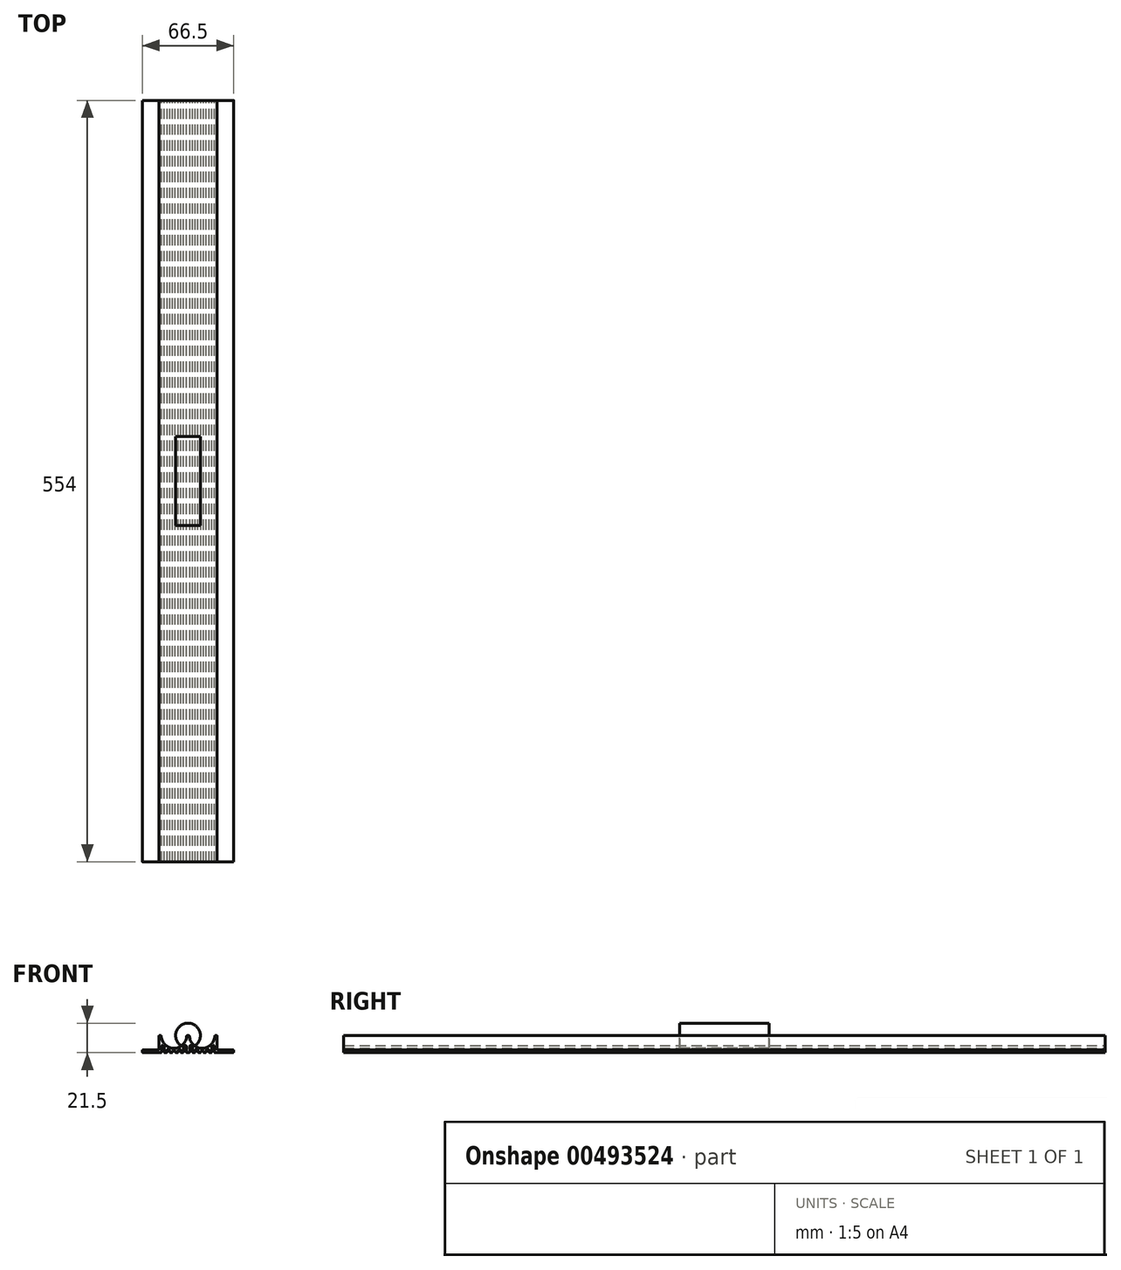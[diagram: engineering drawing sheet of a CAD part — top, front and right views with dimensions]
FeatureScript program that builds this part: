
annotation { "Feature Type Name" : "Feature", "Feature Type Description" : "" }
export const myFeature = defineFeature(function(context is Context, id is Id, definition is map)
    precondition{}
    {
        {
            var Q0;
            Q0=qCreatedBy(makeId("Front.planeOp"),FACE);
            var sketch = newSketch(context, id + "F0", { "sketchPlane" : qUnion([Q0])});
            skArc(sketch, "E0", {"start": v(-19.49, -0.47) * mm, "mid": v(-10.25, -9.25) * mm, "end": v(-1.01, -0.47) * mm});
            skArc(sketch, "E1", {"start": v(-18.38, -7.4) * mm, "mid": v(-17.92, -7.89) * mm, "end": v(-17.42, -8.34) * mm});
            skLineSegment(sketch, "E2", {"start": v(-21.25, -0.5) * mm, "end": v(-21.25, -10) * mm});
            skLineSegment(sketch, "E3", {"start": v(-21.25, -12.5) * mm, "end": v(-19.75, -12.5) * mm});
            skLineSegment(sketch, "E4", {"start": v(-19.25, -7.75) * mm, "end": v(-19.25, -12) * mm});
            skLineSegment(sketch, "E5", {"start": v(-17.25, -8.72) * mm, "end": v(-17.25, -12) * mm});
            skLineSegment(sketch, "E6", {"start": v(-15.25, -10.58) * mm, "end": v(-15.25, -12) * mm});
            skLineSegment(sketch, "E7", {"start": v(-13.25, -10.95) * mm, "end": v(-13.25, -12) * mm});
            skLineSegment(sketch, "E8", {"start": v(-11.25, -11.49) * mm, "end": v(-11.25, -12) * mm});
            skLineSegment(sketch, "E9", {"start": v(-1.25, -7.75) * mm, "end": v(-1.25, -12) * mm});
            skLineSegment(sketch, "E10.trimOffspring", {"start": v(-16.75, -12.5) * mm, "end": v(-15.75, -12.5) * mm});
            skLineSegment(sketch, "E11.trimOffspring", {"start": v(-12.75, -12.5) * mm, "end": v(-11.75, -12.5) * mm});
            skLineSegment(sketch, "E12.trimOffspring", {"start": v(-0.75, -12.5) * mm, "end": v(0, -12.5) * mm});
            skLineSegment(sketch, "E13", {"start": v(-20.75, 0) * mm, "end": v(-19.99, 0) * mm});
            skLineSegment(sketch, "E14", {"start": v(-10.25, 0) * mm, "end": v(0, 0) * mm, "construction": true});
            skArc(sketch, "E15.trimOffspring", {"start": v(-14.55, -10.12) * mm, "mid": v(-14.08, -10.31) * mm, "end": v(-13.6, -10.48) * mm});
            skArc(sketch, "E16.trimOffspring", {"start": v(-10.73, -10.99) * mm, "mid": v(-10.25, -11) * mm, "end": v(-9.77, -10.99) * mm});
            skLineSegment(sketch, "E17", {"start": v(-0.51, 0) * mm, "end": v(0, 0) * mm});
            skLineSegment(sketch, "E18", {"start": v(-9.25, -11.49) * mm, "end": v(-9.25, -12) * mm});
            skLineSegment(sketch, "E19", {"start": v(-8.75, -12.5) * mm, "end": v(-7.75, -12.5) * mm});
            skLineSegment(sketch, "E20", {"start": v(-7.25, -12) * mm, "end": v(-7.25, -10.95) * mm});
            skLineSegment(sketch, "E21", {"start": v(-5.25, -10.58) * mm, "end": v(-5.25, -12) * mm});
            skLineSegment(sketch, "E22", {"start": v(-4.75, -12.5) * mm, "end": v(-3.75, -12.5) * mm});
            skLineSegment(sketch, "E23", {"start": v(-3.25, -12) * mm, "end": v(-3.25, -8.72) * mm});
            skLineSegment(sketch, "E24", {"start": v(-19.25, -12.5) * mm, "end": v(-17.25, -12.5) * mm, "construction": true});
            skLineSegment(sketch, "E25", {"start": v(-15.25, -12.5) * mm, "end": v(-13.25, -12.5) * mm, "construction": true});
            skLineSegment(sketch, "E26", {"start": v(-11.25, -12.5) * mm, "end": v(-9.25, -12.5) * mm, "construction": true});
            skLineSegment(sketch, "E27", {"start": v(-7.25, -12.5) * mm, "end": v(-5.25, -12.5) * mm, "construction": true});
            skLineSegment(sketch, "E28", {"start": v(-3.25, -12.5) * mm, "end": v(-1.25, -12.5) * mm, "construction": true});
            skArc(sketch, "E29.trimOffspring", {"start": v(-6.9, -10.48) * mm, "mid": v(-6.42, -10.31) * mm, "end": v(-5.95, -10.12) * mm});
            skArc(sketch, "E30.trimOffspring", {"start": v(-3.08, -8.34) * mm, "mid": v(-2.58, -7.89) * mm, "end": v(-2.12, -7.4) * mm});
            skLineSegment(sketch, "E31", {"start": v(-21.25, -12.5) * mm, "end": v(-32.75, -12.5) * mm});
            skLineSegment(sketch, "E32", {"start": v(-33.25, -12) * mm, "end": v(-33.25, -11) * mm});
            skLineSegment(sketch, "E33", {"start": v(-32.75, -10.5) * mm, "end": v(-21.75, -10.5) * mm});
            skPoint(sketch, "E34.visualSharp", {"position": v(-21.25, -10.5) * mm});
            skArc(sketch, "E34.filletArc", {"start": v(-21.75, -10.5) * mm, "mid": v(-21.4, -10.35) * mm, "end": v(-21.25, -10) * mm});
            skPoint(sketch, "E35.visualSharp", {"position": v(-19.25, -12.5) * mm});
            skArc(sketch, "E35.filletArc", {"start": v(-19.75, -12.5) * mm, "mid": v(-19.4, -12.35) * mm, "end": v(-19.25, -12) * mm});
            skPoint(sketch, "E36.visualSharp", {"position": v(-17.25, -12.5) * mm});
            skArc(sketch, "E36.filletArc", {"start": v(-17.25, -12) * mm, "mid": v(-17.1, -12.35) * mm, "end": v(-16.75, -12.5) * mm});
            skPoint(sketch, "E37.visualSharp", {"position": v(-19.25, -6.32) * mm});
            skArc(sketch, "E37.filletArc", {"start": v(-18.38, -7.4) * mm, "mid": v(-18.93, -7.28) * mm, "end": v(-19.25, -7.75) * mm});
            skPoint(sketch, "E38.visualSharp", {"position": v(-17.25, -8.49) * mm});
            skArc(sketch, "E38.filletArc", {"start": v(-17.25, -8.72) * mm, "mid": v(-17.3, -8.5) * mm, "end": v(-17.42, -8.34) * mm});
            skPoint(sketch, "E39.visualSharp", {"position": v(-15.25, -9.8) * mm});
            skArc(sketch, "E39.filletArc", {"start": v(-14.55, -10.12) * mm, "mid": v(-15.03, -10.17) * mm, "end": v(-15.25, -10.58) * mm});
            skPoint(sketch, "E40.visualSharp", {"position": v(-13.25, -10.58) * mm});
            skArc(sketch, "E40.filletArc", {"start": v(-13.25, -10.95) * mm, "mid": v(-13.35, -10.66) * mm, "end": v(-13.6, -10.48) * mm});
            skPoint(sketch, "E41.visualSharp", {"position": v(-15.25, -12.5) * mm});
            skArc(sketch, "E41.filletArc", {"start": v(-15.75, -12.5) * mm, "mid": v(-15.4, -12.35) * mm, "end": v(-15.25, -12) * mm});
            skPoint(sketch, "E42.visualSharp", {"position": v(-13.25, -12.5) * mm});
            skArc(sketch, "E42.filletArc", {"start": v(-13.25, -12) * mm, "mid": v(-13.1, -12.35) * mm, "end": v(-12.75, -12.5) * mm});
            skPoint(sketch, "E43.visualSharp", {"position": v(-11.25, -12.5) * mm});
            skArc(sketch, "E43.filletArc", {"start": v(-11.75, -12.5) * mm, "mid": v(-11.4, -12.35) * mm, "end": v(-11.25, -12) * mm});
            skPoint(sketch, "E44.visualSharp", {"position": v(-11.25, -10.95) * mm});
            skArc(sketch, "E44.filletArc", {"start": v(-10.73, -10.99) * mm, "mid": v(-11.1, -11.13) * mm, "end": v(-11.25, -11.49) * mm});
            skPoint(sketch, "E45.visualSharp", {"position": v(-9.25, -10.95) * mm});
            skArc(sketch, "E45.filletArc", {"start": v(-9.25, -11.49) * mm, "mid": v(-9.4, -11.13) * mm, "end": v(-9.77, -10.99) * mm});
            skPoint(sketch, "E46.visualSharp", {"position": v(-9.25, -12.5) * mm});
            skArc(sketch, "E46.filletArc", {"start": v(-9.25, -12) * mm, "mid": v(-9.1, -12.35) * mm, "end": v(-8.75, -12.5) * mm});
            skPoint(sketch, "E47.visualSharp", {"position": v(-7.25, -12.5) * mm});
            skArc(sketch, "E47.filletArc", {"start": v(-7.75, -12.5) * mm, "mid": v(-7.4, -12.35) * mm, "end": v(-7.25, -12) * mm});
            skPoint(sketch, "E48.visualSharp", {"position": v(-7.25, -10.58) * mm});
            skArc(sketch, "E48.filletArc", {"start": v(-6.9, -10.48) * mm, "mid": v(-7.15, -10.66) * mm, "end": v(-7.25, -10.95) * mm});
            skPoint(sketch, "E49.visualSharp", {"position": v(-5.25, -9.8) * mm});
            skArc(sketch, "E49.filletArc", {"start": v(-5.25, -10.58) * mm, "mid": v(-5.47, -10.17) * mm, "end": v(-5.95, -10.12) * mm});
            skPoint(sketch, "E50.visualSharp", {"position": v(-5.25, -12.5) * mm});
            skArc(sketch, "E50.filletArc", {"start": v(-5.25, -12) * mm, "mid": v(-5.1, -12.35) * mm, "end": v(-4.75, -12.5) * mm});
            skPoint(sketch, "E51.visualSharp", {"position": v(-3.25, -12.5) * mm});
            skArc(sketch, "E51.filletArc", {"start": v(-3.75, -12.5) * mm, "mid": v(-3.4, -12.35) * mm, "end": v(-3.25, -12) * mm});
            skPoint(sketch, "E52.visualSharp", {"position": v(-33.25, -12.5) * mm});
            skArc(sketch, "E52.filletArc", {"start": v(-33.25, -12) * mm, "mid": v(-33.1, -12.35) * mm, "end": v(-32.75, -12.5) * mm});
            skPoint(sketch, "E53.visualSharp", {"position": v(-33.25, -10.5) * mm});
            skArc(sketch, "E53.filletArc", {"start": v(-32.75, -10.5) * mm, "mid": v(-33.1, -10.65) * mm, "end": v(-33.25, -11) * mm});
            skPoint(sketch, "E54.visualSharp", {"position": v(-1.25, -12.5) * mm});
            skArc(sketch, "E54.filletArc", {"start": v(-1.25, -12) * mm, "mid": v(-1.1, -12.35) * mm, "end": v(-0.75, -12.5) * mm});
            skPoint(sketch, "E55.visualSharp", {"position": v(-3.25, -8.49) * mm});
            skArc(sketch, "E55.filletArc", {"start": v(-3.08, -8.34) * mm, "mid": v(-3.2, -8.5) * mm, "end": v(-3.25, -8.72) * mm});
            skPoint(sketch, "E56.visualSharp", {"position": v(-1.25, -6.32) * mm});
            skArc(sketch, "E56.filletArc", {"start": v(-1.25, -7.75) * mm, "mid": v(-1.57, -7.28) * mm, "end": v(-2.12, -7.4) * mm});
            skPoint(sketch, "E57.visualSharp", {"position": v(-21.25, 0) * mm});
            skArc(sketch, "E57.filletArc", {"start": v(-20.75, 0) * mm, "mid": v(-21.1, -0.15) * mm, "end": v(-21.25, -0.5) * mm});
            skPoint(sketch, "E58.visualSharp", {"position": v(-19.5, 0) * mm});
            skArc(sketch, "E58.filletArc", {"start": v(-19.49, -0.47) * mm, "mid": v(-19.64, -0.14) * mm, "end": v(-19.99, 0) * mm});
            skPoint(sketch, "E59.visualSharp", {"position": v(-1, 0) * mm});
            skArc(sketch, "E59.filletArc", {"start": v(-0.51, 0) * mm, "mid": v(-0.86, -0.14) * mm, "end": v(-1.01, -0.47) * mm});
            skPoint(sketch, "E60", {"position": v(0, -12.5) * mm});
            skArc(sketch, "E61.MirrorCS", {"start": v(7.75, -12.5) * mm, "mid": v(7.4, -12.35) * mm, "end": v(7.25, -12) * mm});
            skArc(sketch, "E62.MirrorCS", {"start": v(1.25, -12) * mm, "mid": v(1.1, -12.35) * mm, "end": v(0.75, -12.5) * mm});
            skLineSegment(sketch, "E63.MirrorCS", {"start": v(0.75, -12.5) * mm, "end": v(0, -12.5) * mm});
            skLineSegment(sketch, "E64.MirrorCS", {"start": v(9.25, -11.49) * mm, "end": v(9.25, -12) * mm});
            skArc(sketch, "E65.MirrorCS", {"start": v(17.25, -8.72) * mm, "mid": v(17.3, -8.5) * mm, "end": v(17.42, -8.34) * mm});
            skArc(sketch, "E66.MirrorCS", {"start": v(19.49, -0.47) * mm, "mid": v(19.64, -0.14) * mm, "end": v(19.99, 0) * mm});
            skArc(sketch, "E67.MirrorCS", {"start": v(13.25, -12) * mm, "mid": v(13.1, -12.35) * mm, "end": v(12.75, -12.5) * mm});
            skArc(sketch, "E68.MirrorCS", {"start": v(20.75, 0) * mm, "mid": v(21.1, -0.15) * mm, "end": v(21.25, -0.5) * mm});
            skArc(sketch, "E69.MirrorCS", {"start": v(15.75, -12.5) * mm, "mid": v(15.4, -12.35) * mm, "end": v(15.25, -12) * mm});
            skLineSegment(sketch, "E70.MirrorCS", {"start": v(20.75, 0) * mm, "end": v(19.99, 0) * mm});
            skArc(sketch, "E71.MirrorCS", {"start": v(5.25, -12) * mm, "mid": v(5.1, -12.35) * mm, "end": v(4.75, -12.5) * mm});
            skArc(sketch, "E72.MirrorCS", {"start": v(10.73, -10.99) * mm, "mid": v(11.1, -11.13) * mm, "end": v(11.25, -11.49) * mm});
            skArc(sketch, "E73.MirrorCS", {"start": v(0.51, 0) * mm, "mid": v(0.86, -0.14) * mm, "end": v(1.01, -0.47) * mm});
            skArc(sketch, "E74.MirrorCS", {"start": v(21.75, -10.5) * mm, "mid": v(21.4, -10.35) * mm, "end": v(21.25, -10) * mm});
            skLineSegment(sketch, "E75.MirrorCS", {"start": v(8.75, -12.5) * mm, "end": v(7.75, -12.5) * mm});
            skArc(sketch, "E76.MirrorCS", {"start": v(13.25, -10.95) * mm, "mid": v(13.35, -10.66) * mm, "end": v(13.6, -10.48) * mm});
            skArc(sketch, "E77.MirrorCS", {"start": v(6.9, -10.48) * mm, "mid": v(7.15, -10.66) * mm, "end": v(7.25, -10.95) * mm});
            skArc(sketch, "E78.MirrorCS", {"start": v(11.75, -12.5) * mm, "mid": v(11.4, -12.35) * mm, "end": v(11.25, -12) * mm});
            skArc(sketch, "E79.MirrorCS", {"start": v(9.25, -12) * mm, "mid": v(9.1, -12.35) * mm, "end": v(8.75, -12.5) * mm});
            skLineSegment(sketch, "E80.MirrorCS", {"start": v(7.25, -12) * mm, "end": v(7.25, -10.95) * mm});
            skArc(sketch, "E81.MirrorCS", {"start": v(9.25, -11.49) * mm, "mid": v(9.4, -11.13) * mm, "end": v(9.77, -10.99) * mm});
            skArc(sketch, "E82.MirrorCS", {"start": v(3.08, -8.34) * mm, "mid": v(3.2, -8.5) * mm, "end": v(3.25, -8.72) * mm});
            skLineSegment(sketch, "E83.MirrorCS", {"start": v(13.25, -10.95) * mm, "end": v(13.25, -12) * mm});
            skLineSegment(sketch, "E84.MirrorCS", {"start": v(11.25, -11.49) * mm, "end": v(11.25, -12) * mm});
            skArc(sketch, "E85.MirrorCS", {"start": v(32.75, -10.5) * mm, "mid": v(33.1, -10.65) * mm, "end": v(33.25, -11) * mm});
            skLineSegment(sketch, "E86.MirrorCS", {"start": v(4.75, -12.5) * mm, "end": v(3.75, -12.5) * mm});
            skArc(sketch, "E87.MirrorCS", {"start": v(3.75, -12.5) * mm, "mid": v(3.4, -12.35) * mm, "end": v(3.25, -12) * mm});
            skArc(sketch, "E88.MirrorCS", {"start": v(19.75, -12.5) * mm, "mid": v(19.4, -12.35) * mm, "end": v(19.25, -12) * mm});
            skArc(sketch, "E89.MirrorCS", {"start": v(14.55, -10.12) * mm, "mid": v(14.08, -10.31) * mm, "end": v(13.6, -10.48) * mm});
            skLineSegment(sketch, "E90.MirrorCS", {"start": v(21.25, -12.5) * mm, "end": v(19.75, -12.5) * mm});
            skArc(sketch, "E91.MirrorCS", {"start": v(5.25, -10.58) * mm, "mid": v(5.47, -10.17) * mm, "end": v(5.95, -10.12) * mm});
            skArc(sketch, "E92.MirrorCS", {"start": v(18.38, -7.4) * mm, "mid": v(17.92, -7.89) * mm, "end": v(17.42, -8.34) * mm});
            skArc(sketch, "E93.MirrorCS", {"start": v(1.25, -7.75) * mm, "mid": v(1.57, -7.28) * mm, "end": v(2.12, -7.4) * mm});
            skArc(sketch, "E94.MirrorCS", {"start": v(14.55, -10.12) * mm, "mid": v(15.03, -10.17) * mm, "end": v(15.25, -10.58) * mm});
            skArc(sketch, "E95.MirrorCS", {"start": v(3.08, -8.34) * mm, "mid": v(2.58, -7.89) * mm, "end": v(2.12, -7.4) * mm});
            skArc(sketch, "E96.MirrorCS", {"start": v(10.73, -10.99) * mm, "mid": v(10.25, -11) * mm, "end": v(9.77, -10.99) * mm});
            skArc(sketch, "E97.MirrorCS", {"start": v(18.38, -7.4) * mm, "mid": v(18.93, -7.28) * mm, "end": v(19.25, -7.75) * mm});
            skLineSegment(sketch, "E98.MirrorCS", {"start": v(33.25, -12) * mm, "end": v(33.25, -11) * mm});
            skArc(sketch, "E99.MirrorCS", {"start": v(33.25, -12) * mm, "mid": v(33.1, -12.35) * mm, "end": v(32.75, -12.5) * mm});
            skArc(sketch, "E100.MirrorCS", {"start": v(6.9, -10.48) * mm, "mid": v(6.42, -10.31) * mm, "end": v(5.95, -10.12) * mm});
            skLineSegment(sketch, "E101.MirrorCS", {"start": v(0.51, 0) * mm, "end": v(0, 0) * mm});
            skArc(sketch, "E102.MirrorCS", {"start": v(17.25, -12) * mm, "mid": v(17.1, -12.35) * mm, "end": v(16.75, -12.5) * mm});
            skLineSegment(sketch, "E103.MirrorCS", {"start": v(5.25, -10.58) * mm, "end": v(5.25, -12) * mm});
            skLineSegment(sketch, "E104.MirrorCS", {"start": v(15.25, -10.58) * mm, "end": v(15.25, -12) * mm});
            skLineSegment(sketch, "E105.MirrorCS", {"start": v(12.75, -12.5) * mm, "end": v(11.75, -12.5) * mm});
            skLineSegment(sketch, "E106.MirrorCS", {"start": v(16.75, -12.5) * mm, "end": v(15.75, -12.5) * mm});
            skLineSegment(sketch, "E107.MirrorCS", {"start": v(15.25, -12.5) * mm, "end": v(13.25, -12.5) * mm, "construction": true});
            skLineSegment(sketch, "E108.MirrorCS", {"start": v(3.25, -12.5) * mm, "end": v(1.25, -12.5) * mm, "construction": true});
            skLineSegment(sketch, "E109.MirrorCS", {"start": v(19.25, -12.5) * mm, "end": v(17.25, -12.5) * mm, "construction": true});
            skLineSegment(sketch, "E110.MirrorCS", {"start": v(21.25, -12.5) * mm, "end": v(32.75, -12.5) * mm});
            skPoint(sketch, "E111.MirrorP", {"position": v(11.25, -10.95) * mm});
            skPoint(sketch, "E112.MirrorP", {"position": v(33.25, -12.5) * mm});
            skLineSegment(sketch, "E113.MirrorCS", {"start": v(11.25, -12.5) * mm, "end": v(9.25, -12.5) * mm, "construction": true});
            skPoint(sketch, "E114.MirrorP", {"position": v(17.25, -12.5) * mm});
            skPoint(sketch, "E115.MirrorP", {"position": v(1.25, -6.32) * mm});
            skPoint(sketch, "E116.MirrorP", {"position": v(7.25, -10.58) * mm});
            skPoint(sketch, "E117.MirrorP", {"position": v(13.25, -10.58) * mm});
            skLineSegment(sketch, "E118.MirrorCS", {"start": v(10.25, 0) * mm, "end": v(0, 0) * mm, "construction": true});
            skPoint(sketch, "E119.MirrorP", {"position": v(17.25, -8.49) * mm});
            skPoint(sketch, "E120.MirrorP", {"position": v(15.25, -9.8) * mm});
            skPoint(sketch, "E121.MirrorP", {"position": v(33.25, -10.5) * mm});
            skLineSegment(sketch, "E122.MirrorCS", {"start": v(32.75, -10.5) * mm, "end": v(21.75, -10.5) * mm});
            skPoint(sketch, "E123.MirrorP", {"position": v(3.25, -8.49) * mm});
            skPoint(sketch, "E124.MirrorP", {"position": v(9.25, -10.95) * mm});
            skLineSegment(sketch, "E125.MirrorCS", {"start": v(17.25, -8.72) * mm, "end": v(17.25, -12) * mm});
            skLineSegment(sketch, "E126.MirrorCS", {"start": v(19.25, -7.75) * mm, "end": v(19.25, -12) * mm});
            skPoint(sketch, "E127.MirrorP", {"position": v(13.25, -12.5) * mm});
            skPoint(sketch, "E128.MirrorP", {"position": v(19.5, 0) * mm});
            skArc(sketch, "E129.MirrorCS", {"start": v(19.49, -0.47) * mm, "mid": v(10.25, -9.25) * mm, "end": v(1.01, -0.47) * mm});
            skPoint(sketch, "E130.MirrorP", {"position": v(19.25, -12.5) * mm});
            skLineSegment(sketch, "E131.MirrorCS", {"start": v(3.25, -12) * mm, "end": v(3.25, -8.72) * mm});
            skPoint(sketch, "E132.MirrorP", {"position": v(9.25, -12.5) * mm});
            skPoint(sketch, "E133.MirrorP", {"position": v(5.25, -12.5) * mm});
            skPoint(sketch, "E134.MirrorP", {"position": v(15.25, -12.5) * mm});
            skPoint(sketch, "E135.MirrorP", {"position": v(5.25, -9.8) * mm});
            skPoint(sketch, "E136.MirrorP", {"position": v(21.25, 0) * mm});
            skPoint(sketch, "E137.MirrorP", {"position": v(21.25, -10.5) * mm});
            skPoint(sketch, "E138.MirrorP", {"position": v(11.25, -12.5) * mm});
            skPoint(sketch, "E139.MirrorP", {"position": v(1, 0) * mm});
            skLineSegment(sketch, "E140.MirrorCS", {"start": v(21.25, -0.5) * mm, "end": v(21.25, -10) * mm});
            skPoint(sketch, "E141.MirrorP", {"position": v(3.25, -12.5) * mm});
            skPoint(sketch, "E142.MirrorP", {"position": v(1.25, -12.5) * mm});
            skPoint(sketch, "E143.MirrorP", {"position": v(19.25, -6.32) * mm});
            skLineSegment(sketch, "E144.MirrorCS", {"start": v(7.25, -12.5) * mm, "end": v(5.25, -12.5) * mm, "construction": true});
            skPoint(sketch, "E145.MirrorP", {"position": v(7.25, -12.5) * mm});
            skLineSegment(sketch, "E146.MirrorCS", {"start": v(1.25, -7.75) * mm, "end": v(1.25, -12) * mm});
            skSolve(sketch);
        }
        {
            var Q0;
            Q0 = qSketchRegion(id + "F0", true);
            extrude(context, id + "F1", {"entities" : qUnion([Q0]), "depth" : 554 * mm, "symmetric" : true});
        }
        {
            var Q0;
            Q0=qCreatedBy(makeId("Front.planeOp"),FACE);
            var sketch = newSketch(context, id + "F2", { "sketchPlane" : qUnion([Q0])});
            skCircle(sketch, "E147", {"center": v(0, 0) * mm, "radius": 9 * mm});
            skSolve(sketch);
        }
        {
            var Q0;
            Q0 = qSketchRegion(id + "F2", true);
            extrude(context, id + "F3", {"entities" : qUnion([Q0]), "depth" : 65 * mm, "symmetric" : true});
        }
    });
